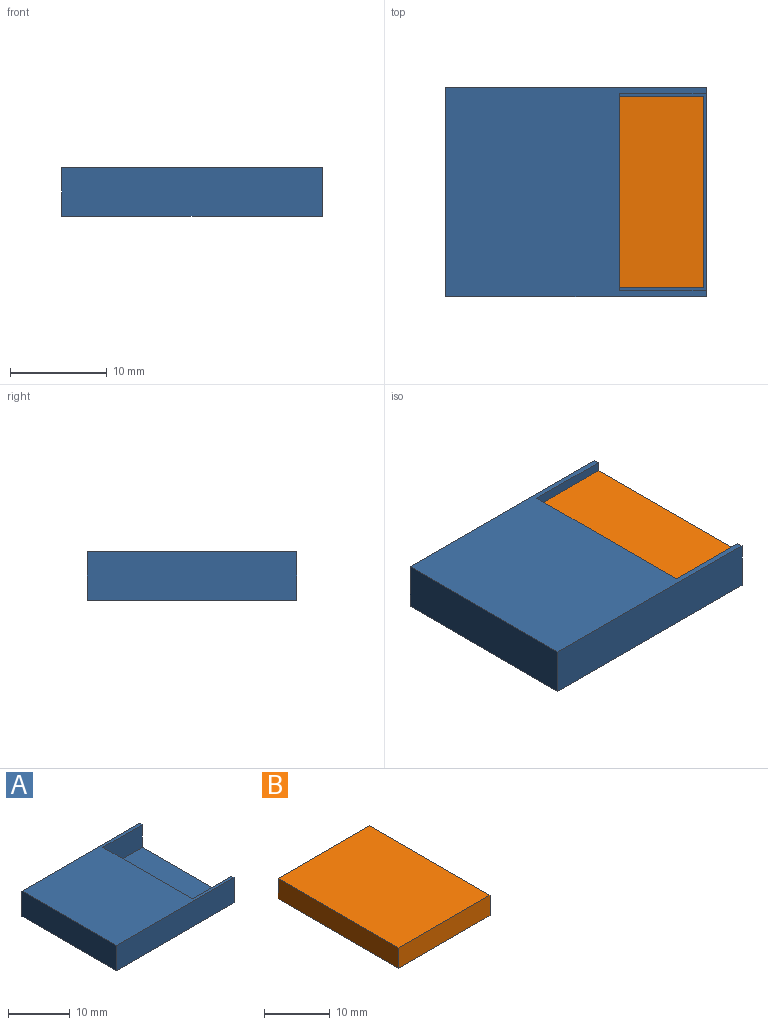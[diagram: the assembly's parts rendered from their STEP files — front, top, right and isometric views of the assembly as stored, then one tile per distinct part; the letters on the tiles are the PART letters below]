
ASSEMBLY  parts=2 mates=1
PART A: 14 faces, bbox 26.9x21.7x5 mm
  f0: plane 20.45x0.57mm, normal (1,0,0), area 11.7mm2, adj f1,f7,f8,f12
  f1: plane 26.92x21.65mm, normal (0,0,1), area 399.4mm2, adj f0,f2,f3,f4,f5,f7,f8
  f2: plane 21.65x5mm, normal (-1,0,0), area 108.2mm2, adj f1,f3,f5,f6
  f3: plane 26.92x5mm, normal (0,-1,0), area 134.6mm2, adj f1,f2,f4,f6
  f4: plane 21.65x5mm, normal (1,0,0), area 16.7mm2, adj f1,f3,f5,f6,f7,f8,f9
  f5: plane 26.92x5mm, normal (0,1,0), area 134.6mm2, adj f1,f2,f4,f6
  f6: plane 26.92x21.65mm, normal (0,0,-1), area 582.8mm2, adj f2,f3,f4,f5
  f7: plane 26.32x4.52mm, normal (0,-1,0), area 108.7mm2, adj f0,f1,f4,f9,f10,f11,f12,f13
  f8: plane 26.32x4.52mm, normal (0,1,0), area 108.7mm2, adj f0,f1,f4,f9,f10,f11,f12,f13
  f9: plane 20.45x8.97mm, normal (0,0,1), area 183.4mm2, adj f4,f7,f8,f10
  f10: plane 20.45x0.05mm, normal (-1,0,0), area 1mm2, adj f7,f8,f9,f11
  f11: plane 20.45x17.35mm, normal (0,0,1), area 354.8mm2, adj f7,f8,f10,f13
  f12: plane 20.45x17.35mm, normal (0,0,-1), area 354.8mm2, adj f0,f7,f8,f13
  f13: plane 20.45x3.95mm, normal (1,0,0), area 80.8mm2, adj f7,f8,f11,f12
PART B: 6 faces, bbox 19.8x26x3.8 mm
  f0: plane 26.02x3.8mm, normal (-1,0,0), area 98.9mm2, adj f1,f3,f4,f5
  f1: plane 19.75x3.8mm, normal (0,-1,0), area 75mm2, adj f0,f2,f4,f5
  f2: plane 26.02x3.8mm, normal (1,0,0), area 98.9mm2, adj f1,f3,f4,f5
  f3: plane 19.75x3.8mm, normal (0,1,0), area 75mm2, adj f0,f2,f4,f5
  f4: plane 26.02x19.75mm, normal (0,0,1), area 513.9mm2, adj f0,f1,f2,f3
  f5: plane 26.02x19.75mm, normal (0,0,-1), area 513.9mm2, adj f0,f1,f2,f3
PLACE A t=(0,0,-0.31)mm
PLACE B rot(axis=(0,0,1),90deg) t=(26.62,0.95,0.24)mm
MATE fastened B.f3 <-> A.f13  axis (-1,0,0) through (0.6,10.82,2.14)mm
